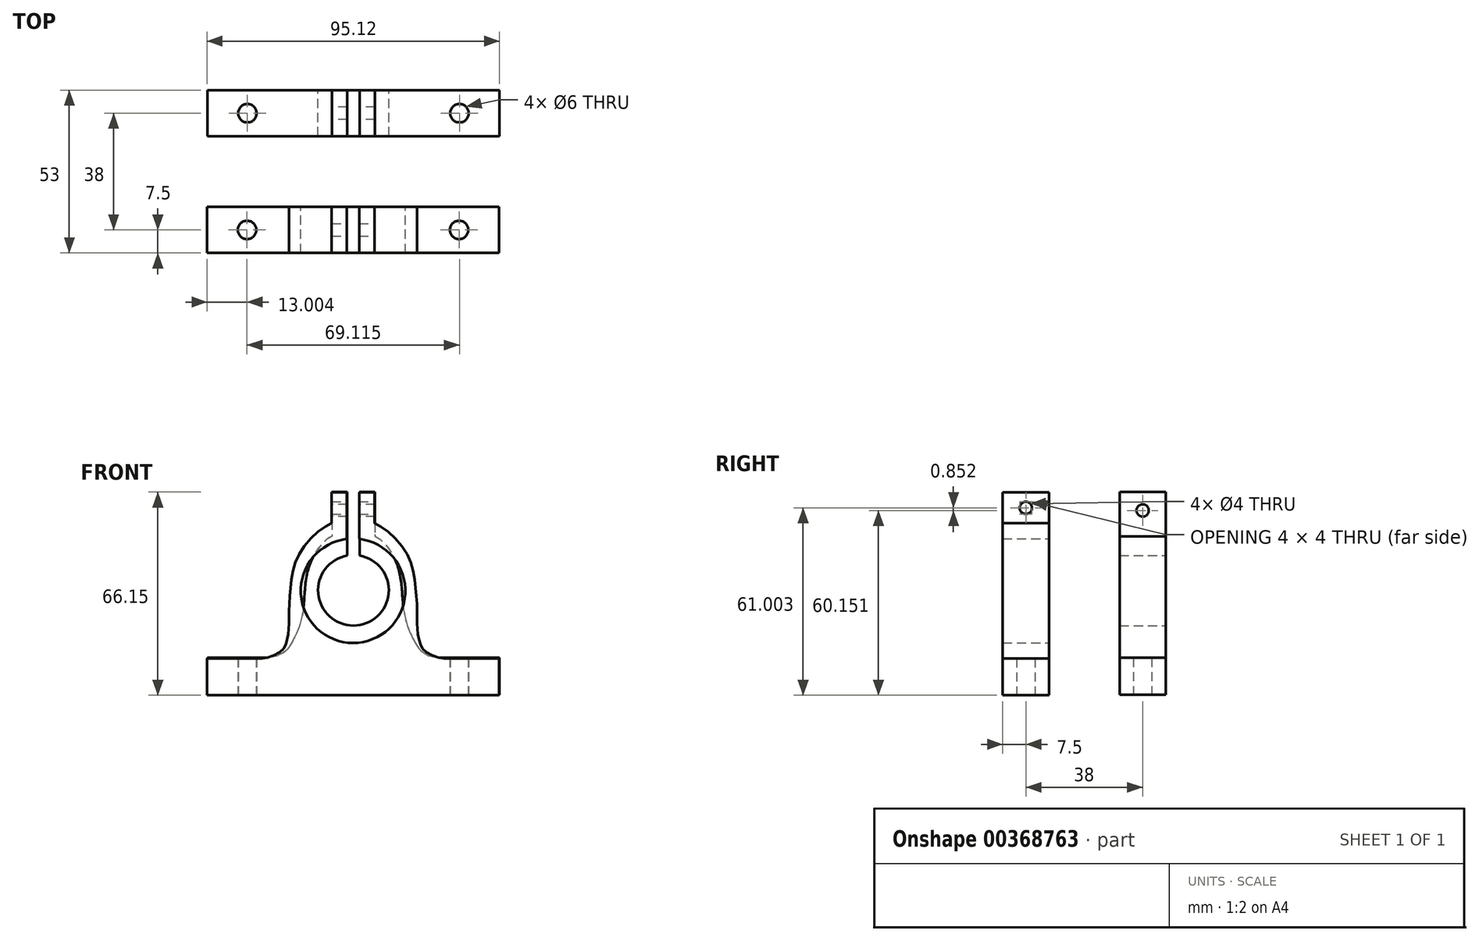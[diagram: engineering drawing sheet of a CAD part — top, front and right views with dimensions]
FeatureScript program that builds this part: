
annotation { "Feature Type Name" : "Feature", "Feature Type Description" : "" }
export const myFeature = defineFeature(function(context is Context, id is Id, definition is map)
    precondition{}
    {
        {
            var Q0;
            Q0=qCreatedBy(makeId("Front.planeOp"),FACE);
            var sketch = newSketch(context, id + "F0", { "sketchPlane" : qUnion([Q0])});
            skLineSegment(sketch, "E0", {"start": v(-125.67, 107.47) * mm, "end": v(-132.67, 107.47) * mm});
            skLineSegment(sketch, "E1", {"start": v(-132.67, 107.47) * mm, "end": v(-132.67, 93.08) * mm});
            skFitSpline(sketch, "E2", {"points": [v(-132.67, 93.08) * mm, v(-138.51, 86.87) * mm, v(-141.25, 77.79) * mm, v(-142.11, 68.36) * mm, v(-143.95, 62.03) * mm, v(-145.67, 58.6) * mm, v(-148.95, 54.77) * mm, v(-155.17, 53.47) * mm], "startDerivative": vector(-41.03, -17.29) * mm, "endDerivative": vector(-26.14, 0) * mm});
            skLineSegment(sketch, "E3", {"start": v(-155.17, 53.47) * mm, "end": v(-173.17, 53.47) * mm});
            skLineSegment(sketch, "E4", {"start": v(-173.17, 53.47) * mm, "end": v(-173.17, 41.47) * mm});
            skLineSegment(sketch, "E5", {"start": v(-173.17, 41.47) * mm, "end": v(-125.67, 41.47) * mm});
            skLineSegment(sketch, "E6", {"start": v(-125.67, 41.47) * mm, "end": v(-125.67, 63.97) * mm});
            skArc(sketch, "E7", {"start": v(-125.67, 86.97) * mm, "mid": v(-137.17, 75.47) * mm, "end": v(-125.67, 63.97) * mm});
            skLineSegment(sketch, "E8", {"start": v(-125.67, 86.97) * mm, "end": v(-125.67, 107.47) * mm});
            skPoint(sketch, "E9", {"position": v(-160.17, 53.47) * mm});
            skLineSegment(sketch, "E10", {"start": v(-125.67, 134.36) * mm, "end": v(-125.67, 3.27) * mm, "construction": true});
            skLineSegment(sketch, "E11.MirrorCS", {"start": v(-125.67, 107.47) * mm, "end": v(-118.67, 107.47) * mm});
            skArc(sketch, "E12.MirrorCS", {"start": v(-125.67, 86.97) * mm, "mid": v(-114.17, 75.47) * mm, "end": v(-125.67, 63.97) * mm});
            skLineSegment(sketch, "E13.MirrorCS", {"start": v(-78.17, 53.47) * mm, "end": v(-78.17, 41.47) * mm});
            skLineSegment(sketch, "E14.MirrorCS", {"start": v(-96.17, 53.47) * mm, "end": v(-78.17, 53.47) * mm});
            skLineSegment(sketch, "E15.MirrorCS", {"start": v(-78.17, 41.47) * mm, "end": v(-125.67, 41.47) * mm});
            skLineSegment(sketch, "E16.MirrorCS", {"start": v(-118.67, 107.47) * mm, "end": v(-118.67, 93.08) * mm});
            skFitSpline(sketch, "E17.MirrorCS", {"points": [v(-118.67, 93.08) * mm, v(-112.83, 86.87) * mm, v(-110.09, 77.79) * mm, v(-109.23, 68.36) * mm, v(-107.4, 62.03) * mm, v(-105.67, 58.6) * mm, v(-102.39, 54.77) * mm, v(-96.17, 53.47) * mm], "startDerivative": vector(41.03, -17.29) * mm, "endDerivative": vector(26.14, 0) * mm});
            skPoint(sketch, "E18.MirrorP", {"position": v(-91.17, 53.47) * mm});
            skSolve(sketch);
        }
        {
            var Q0;
            Q0 = qSketchRegion(id + "F0", true);
            extrude(context, id + "F1", {"entities" : qUnion([Q0]), "depth" : 15 * mm, "offsetDistance" : 25 * mm});
        }
        {
            var Q0;
            Q0=qCreatedBy(makeId("Front.planeOp"),FACE);
            cPlane(context, id + "F2", {"entities" : qUnion([Q0]), "cplaneType" : CPlaneType.OFFSET, "offset" : 38 * mm, "width" : 150 * mm, "height" : 150 * mm});
        }
        {
            var Q0;
            Q0=makeQuery(id+"F1.opExtrude","SWEPT_FACE",FACE,{"disambiguationData":[OSD([sQuery(id+"F0.wireOp",EDGE,"E0"),sQuery(id+"F0.wireOp",EDGE,"E11.MirrorCS")])]});
            var sketch = newSketch(context, id + "F3", { "sketchPlane" : qUnion([Q0])});
            skLineSegment(sketch, "E19.bottom", {"start": v(-127.67, 0) * mm, "end": v(-123.67, 0) * mm});
            skLineSegment(sketch, "E19.top", {"start": v(-127.67, -15) * mm, "end": v(-123.67, -15) * mm});
            skLineSegment(sketch, "E19.left", {"start": v(-127.67, 0) * mm, "end": v(-127.67, -15) * mm});
            skLineSegment(sketch, "E19.right", {"start": v(-123.67, 0) * mm, "end": v(-123.67, -15) * mm});
            skPoint(sketch, "E20", {"position": v(-125.67, 0) * mm});
            skSolve(sketch);
        }
        {
            var Q0;
            Q0 = qSketchRegion(id + "F3", true);
            extrude(context, id + "F4", {"entities" : qUnion([Q0]), "operationType" : NewBodyOperationType.REMOVE, "oppositeDirection" : true, "depth" : 25 * mm, "offsetDistance" : 25 * mm});
        }
        {
            var Q0;
            Q0=makeQuery(id+"F1.opExtrude","SWEPT_FACE",FACE,{"disambiguationData":[OSD([sQuery(id+"F0.wireOp",EDGE,"E5"),sQuery(id+"F0.wireOp",EDGE,"E15.MirrorCS")])]});
            var sketch = newSketch(context, id + "F5", { "sketchPlane" : qUnion([Q0])});
            skCircle(sketch, "E21", {"center": v(-160.17, 7.5) * mm, "radius": 3 * mm});
            skPoint(sketch, "E21.centerSnap0", {"position": v(-173.17, 7.5) * mm});
            skCircle(sketch, "E22", {"center": v(-91.17, 7.5) * mm, "radius": 3 * mm});
            skSolve(sketch);
        }
        {
            var Q0;
            Q0=makeQuery(id+"F5.imprint","IMPRINT",FACE,{"disambiguationData":[TD([[makeQuery(id+"F5.imprint","IMPRINT",EDGE,{"derivedFrom":sQuery(id+"F5.wireOp",EDGE,"E21")}),1.0]])]});
            var Q1;
            Q1=makeQuery(id+"F5.imprint","IMPRINT",FACE,{"disambiguationData":[TD([[makeQuery(id+"F5.imprint","IMPRINT",EDGE,{"derivedFrom":sQuery(id+"F5.wireOp",EDGE,"E22")}),1.0]])]});
            extrude(context, id + "F6", {"entities" : qUnion([Q0, Q1]), "operationType" : NewBodyOperationType.REMOVE, "oppositeDirection" : true, "depth" : 25 * mm, "offsetDistance" : 25 * mm});
        }
        {
            var Q0;
            Q0=makeQuery(id+"F1.opExtrude","SWEPT_FACE",FACE,{"disambiguationData":[OSD([sQuery(id+"F0.wireOp",EDGE,"E1")])]});
            var sketch = newSketch(context, id + "F7", { "sketchPlane" : qUnion([Q0])});
            skCircle(sketch, "E23", {"center": v(7.5, 101.47) * mm, "radius": 2 * mm});
            skPoint(sketch, "E23.centerSnap0", {"position": v(7.5, 107.47) * mm});
            skSolve(sketch);
        }
        {
            var Q0;
            Q0 = qSketchRegion(id + "F11", true);
            var Q1;
            Q1=makeQuery(id+"F7.imprint","IMPRINT",FACE,{"disambiguationData":[TD([[makeQuery(id+"F7.imprint","IMPRINT",EDGE,{"derivedFrom":sQuery(id+"F7.wireOp",EDGE,"E23")}),1.0]])]});
            extrude(context, id + "F8", {"entities" : qUnion([Q0, Q1]), "operationType" : NewBodyOperationType.REMOVE, "oppositeDirection" : true, "depth" : 25 * mm, "offsetDistance" : 25 * mm});
        }
        {
            var Q0;
            Q0=qCreatedBy(id+"F2.planeOp",FACE);
            var sketch = newSketch(context, id + "F9", { "sketchPlane" : qUnion([Q0])});
            skLineSegment(sketch, "E24", {"start": v(-125.79, 107.32) * mm, "end": v(-132.79, 107.32) * mm});
            skLineSegment(sketch, "E25", {"start": v(-132.79, 107.32) * mm, "end": v(-132.79, 97.32) * mm});
            skFitSpline(sketch, "E26", {"points": [v(-132.79, 97.32) * mm, v(-142.31, 89.05) * mm, v(-146.01, 77.33) * mm, v(-146.66, 68.23) * mm, v(-146.72, 62.68) * mm, v(-147.5, 58.4) * mm, v(-149.79, 55.22) * mm, v(-155.29, 53.32) * mm], "startDerivative": vector(-41.03, -17.29) * mm, "endDerivative": vector(-26.14, 0) * mm});
            skLineSegment(sketch, "E27", {"start": v(-155.29, 53.32) * mm, "end": v(-173.29, 53.32) * mm});
            skLineSegment(sketch, "E28", {"start": v(-173.29, 53.32) * mm, "end": v(-173.29, 41.32) * mm});
            skLineSegment(sketch, "E29", {"start": v(-173.29, 41.32) * mm, "end": v(-125.79, 41.32) * mm});
            skLineSegment(sketch, "E30", {"start": v(-125.79, 41.32) * mm, "end": v(-125.79, 58.32) * mm});
            skArc(sketch, "E31", {"start": v(-125.79, 92.32) * mm, "mid": v(-142.79, 75.32) * mm, "end": v(-125.79, 58.32) * mm});
            skLineSegment(sketch, "E32", {"start": v(-125.79, 92.32) * mm, "end": v(-125.79, 107.32) * mm});
            skPoint(sketch, "E33", {"position": v(-160.29, 53.32) * mm});
            skLineSegment(sketch, "E34", {"start": v(-125.79, 132.56) * mm, "end": v(-125.79, 26.34) * mm, "construction": true});
            skLineSegment(sketch, "E35.MirrorCS", {"start": v(-118.79, 107.32) * mm, "end": v(-118.79, 97.32) * mm});
            skLineSegment(sketch, "E36.MirrorCS", {"start": v(-78.29, 53.32) * mm, "end": v(-78.29, 41.32) * mm});
            skLineSegment(sketch, "E37.MirrorCS", {"start": v(-96.29, 53.32) * mm, "end": v(-78.29, 53.32) * mm});
            skLineSegment(sketch, "E38.MirrorCS", {"start": v(-125.79, 107.32) * mm, "end": v(-118.79, 107.32) * mm});
            skLineSegment(sketch, "E39.MirrorCS", {"start": v(-78.29, 41.32) * mm, "end": v(-125.79, 41.32) * mm});
            skArc(sketch, "E40.MirrorCS", {"start": v(-125.79, 92.32) * mm, "mid": v(-108.79, 75.32) * mm, "end": v(-125.79, 58.32) * mm});
            skFitSpline(sketch, "E41.MirrorCS", {"points": [v(-118.79, 97.32) * mm, v(-109.26, 89.05) * mm, v(-105.56, 77.33) * mm, v(-104.91, 68.23) * mm, v(-104.85, 62.68) * mm, v(-104.07, 58.4) * mm, v(-101.79, 55.22) * mm, v(-96.29, 53.32) * mm], "startDerivative": vector(41.03, -17.29) * mm, "endDerivative": vector(26.14, 0) * mm});
            skPoint(sketch, "E42.MirrorP", {"position": v(-91.29, 53.32) * mm});
            skSolve(sketch);
        }
        {
            var Q0;
            Q0 = qSketchRegion(id + "F9", true);
            extrude(context, id + "F10", {"entities" : qUnion([Q0]), "depth" : 15 * mm, "offsetDistance" : 25 * mm});
        }
        {
            var Q0;
            Q0=makeQuery(id+"F10.opExtrude","SWEPT_FACE",FACE,{"disambiguationData":[OSD([sQuery(id+"F9.wireOp",EDGE,"E29"),sQuery(id+"F9.wireOp",EDGE,"E39.MirrorCS")])]});
            var sketch = newSketch(context, id + "F11", { "sketchPlane" : qUnion([Q0])});
            skPoint(sketch, "E43", {"position": v(-173.29, 45.5) * mm});
            skCircle(sketch, "E44", {"center": v(-160.29, 45.5) * mm, "radius": 3 * mm});
            skCircle(sketch, "E45", {"center": v(-91.29, 45.5) * mm, "radius": 3 * mm});
            skSolve(sketch);
        }
        {
            var Q0;
            Q0 = qSketchRegion(id + "F11", true);
            extrude(context, id + "F12", {"entities" : qUnion([Q0]), "operationType" : NewBodyOperationType.REMOVE, "oppositeDirection" : true, "depth" : 25 * mm, "offsetDistance" : 25 * mm});
        }
        {
            var Q0;
            Q0=makeQuery(id+"F10.opExtrude","SWEPT_FACE",FACE,{"disambiguationData":[OSD([sQuery(id+"F9.wireOp",EDGE,"E24"),sQuery(id+"F9.wireOp",EDGE,"E38.MirrorCS")])]});
            var sketch = newSketch(context, id + "F13", { "sketchPlane" : qUnion([Q0])});
            skLineSegment(sketch, "E46.bottom", {"start": v(-127.79, -38) * mm, "end": v(-123.79, -38) * mm});
            skLineSegment(sketch, "E46.top", {"start": v(-127.79, -53) * mm, "end": v(-123.79, -53) * mm});
            skLineSegment(sketch, "E46.left", {"start": v(-127.79, -38) * mm, "end": v(-127.79, -53) * mm});
            skLineSegment(sketch, "E46.right", {"start": v(-123.79, -38) * mm, "end": v(-123.79, -53) * mm});
            skPoint(sketch, "E47", {"position": v(-125.79, -38) * mm});
            skSolve(sketch);
        }
        {
            var Q0;
            Q0=makeQuery(id+"F13.imprint","IMPRINT",FACE,{"disambiguationData":[TD([[makeQuery(id+"F13.imprint","IMPRINT",EDGE,{"derivedFrom":sQuery(id+"F13.wireOp",EDGE,"E46.bottom")}),1.0]])]});
            extrude(context, id + "F14", {"entities" : qUnion([Q0]), "operationType" : NewBodyOperationType.REMOVE, "oppositeDirection" : true, "depth" : 25 * mm, "offsetDistance" : 25 * mm});
        }
        {
            var Q0;
            Q0=makeQuery(id+"F10.opExtrude","SWEPT_FACE",FACE,{"disambiguationData":[OSD([sQuery(id+"F9.wireOp",EDGE,"E35.MirrorCS")])]});
            var sketch = newSketch(context, id + "F15", { "sketchPlane" : qUnion([Q0])});
            skCircle(sketch, "E48", {"center": v(-45.5, 102.32) * mm, "radius": 2 * mm});
            skPoint(sketch, "E48.centerSnap0", {"position": v(-45.5, 107.32) * mm});
            skSolve(sketch);
        }
        {
            var Q0;
            Q0 = qSketchRegion(id + "F15", true);
            extrude(context, id + "F16", {"entities" : qUnion([Q0]), "operationType" : NewBodyOperationType.REMOVE, "oppositeDirection" : true, "depth" : 25 * mm, "offsetDistance" : 25 * mm});
        }
    });
